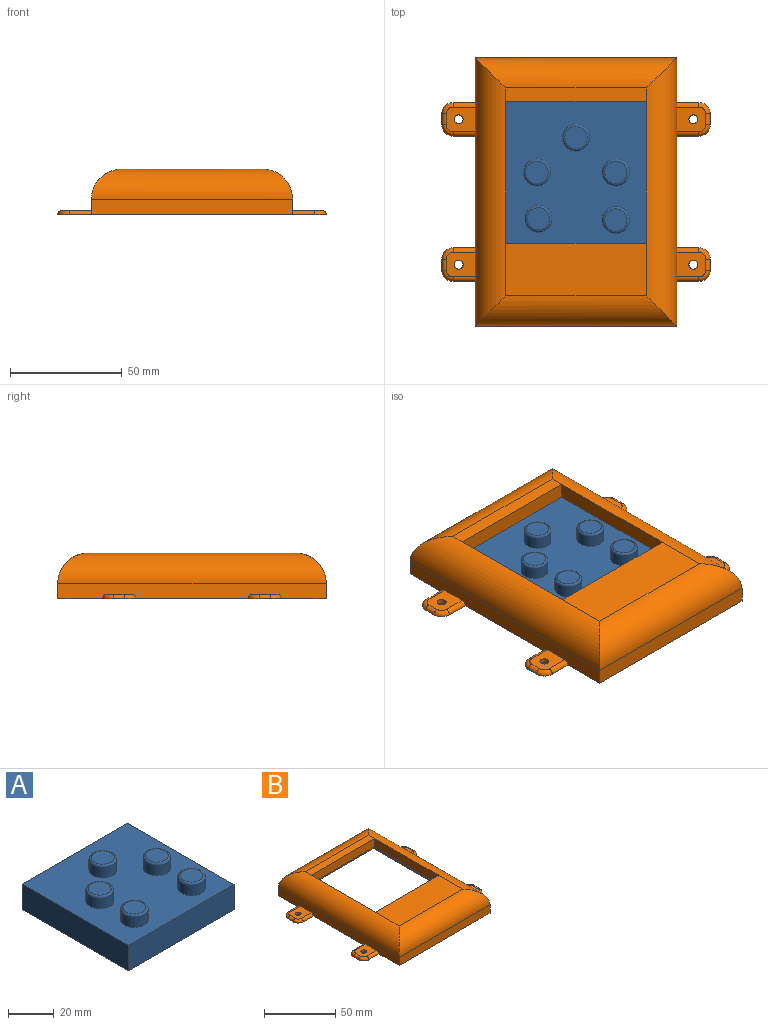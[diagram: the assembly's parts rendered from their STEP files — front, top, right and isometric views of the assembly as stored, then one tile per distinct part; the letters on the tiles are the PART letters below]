
ASSEMBLY  parts=2 mates=1
PART A: 21 faces, bbox 65x65.5x20 mm
  f0: plane 65x13.5mm, normal (0,1,0), area 877.5mm2, adj f1,f3,f4,f5
  f1: plane 65.5x13.5mm, normal (-1,0,0), area 884.3mm2, adj f0,f2,f4,f5
  f2: plane 65x13.5mm, normal (0,-1,0), area 877.5mm2, adj f1,f3,f4,f5
  f3: plane 65.5x13.5mm, normal (1,0,0), area 884.3mm2, adj f0,f2,f4,f5
  f4: plane 65.5x65mm, normal (0,0,1), area 3692mm2, adj f0,f1,f2,f3,f6,f8,f10,f12
  f5: plane 65.5x65mm, normal (0,0,-1), area 4257.5mm2, adj f0,f1,f2,f3
  f6: cylinder r=6mm len=12mm, axis (0,0,-1), area 207.3mm2, adj f4,f20
  f7: plane 10x10mm, normal (0,0,1), area 78.5mm2, adj f20
  f8: cylinder r=6mm len=12mm, axis (0,0,-1), area 207.3mm2, adj f4,f19
  f9: plane 10x10mm, normal (0,0,1), area 78.5mm2, adj f19
  f10: cylinder r=6mm len=12mm, axis (0,0,-1), area 207.3mm2, adj f4,f18
  f11: plane 10x10mm, normal (0,0,1), area 78.5mm2, adj f18
  f12: cylinder r=6mm len=12mm, axis (0,0,-1), area 207.3mm2, adj f4,f17
  f13: plane 10x10mm, normal (0,0,1), area 78.5mm2, adj f17
  f14: cylinder r=6mm len=12mm, axis (0,0,-1), area 207.3mm2, adj f4,f16
  f15: plane 10x10mm, normal (0,0,1), area 78.5mm2, adj f16
  f16: torus R=5mm, axis (0,0,1), area 55.6mm2, adj f14,f15
  f17: torus R=5mm, axis (0,0,1), area 55.6mm2, adj f12,f13
  f18: torus R=5mm, axis (0,0,1), area 55.6mm2, adj f10,f11
  f19: torus R=5mm, axis (0,0,1), area 55.6mm2, adj f8,f9
  f20: torus R=5mm, axis (0,0,1), area 55.6mm2, adj f6,f7
PART B: 63 faces, bbox 120.8x120x21.9 mm
  f0: plane 120x7mm, normal (-1,0,0), area 783.4mm2, adj f1,f13,f14,f18,f53,f54,f55,f56
  f1: plane 120x120mm, normal (0,0,-1), area 1630.8mm2, adj f0,f2,f13,f14,f27,f28,f29,f30
  f2: plane 120x7mm, normal (1,0,0), area 783.4mm2, adj f1,f13,f14,f19,f35,f36,f39,f43
  f3: plane 63x23.5mm, normal (0,0,1), area 1480.5mm2, adj f8,f18,f19,f20
  f4: plane 65x2mm, normal (0,1,0), area 130mm2, adj f5,f7,f15,f16
  f5: plane 65.5x2mm, normal (1,0,0), area 131mm2, adj f4,f6,f15,f16
  f6: plane 65x2mm, normal (0,-1,0), area 130mm2, adj f5,f7,f15,f16
  f7: plane 65.5x2mm, normal (-1,0,0), area 131mm2, adj f4,f6,f15,f16
  f8: plane 63x7mm, normal (0,1,0), area 441mm2, adj f3,f9,f11,f15
  f9: plane 63.5x7mm, normal (-1,0,0), area 444.5mm2, adj f8,f10,f15,f19
  f10: plane 63x7mm, normal (0,-1,0), area 441mm2, adj f9,f11,f12,f15
  f11: plane 63.5x7mm, normal (1,0,0), area 444.5mm2, adj f8,f10,f15,f18
  f12: plane 63x6mm, normal (0,0,1), area 378mm2, adj f10,f17,f18,f19
  f13: plane 90x7mm, normal (0,1,0), area 630mm2, adj f0,f1,f2,f17
  f14: plane 90x7mm, normal (0,-1,0), area 630mm2, adj f0,f1,f2,f20
  f15: plane 65.5x65mm, normal (0,0,-1), area 257mm2, adj f4,f5,f6,f7,f8,f9,f10,f11
  f16: plane 67.5x67mm, normal (0,0,-1), area 265mm2, adj f4,f5,f6,f7,f22,f23,f24,f25
  f17: cylinder r=13.5mm len=90mm, axis (1,0,0), area 1700.5mm2, adj f12,f13,f18,f19
  f18: cylinder r=13.5mm len=120mm, axis (0,1,0), area 2336.6mm2, adj f0,f3,f11,f12,f17,f20
  f19: cylinder r=13.5mm len=120mm, axis (0,-1,0), area 2336.6mm2, adj f2,f3,f9,f12,f17,f20
  f20: cylinder r=13.5mm len=90mm, axis (-1,0,0), area 1700.5mm2, adj f3,f14,f18,f19
  f21: plane 63x21.5mm, normal (0,0,-1), area 1354.5mm2, adj f22,f32,f33,f34
  f22: plane 67x7mm, normal (0,-1,0), area 468.8mm2, adj f16,f21,f23,f25,f32,f33
  f23: plane 67.5x6.82mm, normal (1,0,0), area 460.7mm2, adj f16,f22,f24,f33
  f24: plane 67x7mm, normal (0,1,0), area 468.8mm2, adj f16,f23,f25,f26,f32,f33
  f25: plane 67.5x6.82mm, normal (-1,0,0), area 460.7mm2, adj f16,f22,f24,f32
  f26: plane 63x4mm, normal (0,0,-1), area 252mm2, adj f24,f31,f32,f33
  f27: plane 86x7mm, normal (0,-1,0), area 602mm2, adj f1,f28,f30,f31
  f28: plane 116x7mm, normal (1,0,0), area 812mm2, adj f1,f27,f29,f32
  f29: plane 86x7mm, normal (0,1,0), area 602mm2, adj f1,f28,f30,f34
  f30: plane 116x7mm, normal (-1,0,0), area 812mm2, adj f1,f27,f29,f33
  f31: cylinder r=11.5mm len=86mm, axis (1,0,0), area 1402.5mm2, adj f26,f27,f32,f33
  f32: cylinder r=11.5mm len=116mm, axis (0,1,0), area 1808.8mm2, adj f21,f22,f24,f25,f26,f28,f31,f34
  f33: cylinder r=11.5mm len=116mm, axis (0,-1,0), area 1808.8mm2, adj f21,f22,f23,f24,f26,f30,f31,f34
  f34: cylinder r=11.5mm len=86mm, axis (-1,0,0), area 1402.5mm2, adj f21,f29,f32,f33
  f35: plane 13x11mm, normal (0,0,1), area 126.6mm2, adj f2,f38,f39,f40,f41,f42,f43
  f36: plane 13x11mm, normal (0,0,1), area 126.6mm2, adj f2,f37,f44,f45,f46,f47,f48
  f37: cylinder r=2mm len=4mm, axis (0,0,1), area 25.1mm2, adj f1,f36
  f38: cylinder r=2mm len=4mm, axis (0,0,1), area 25.1mm2, adj f1,f35
  f39: cylinder r=2mm len=10mm, axis (-1,0,0), area 31.4mm2, adj f1,f2,f35,f40
  f40: torus R=3mm, axis (0,0,1), area 21.1mm2, adj f1,f35,f39,f41
  f41: cylinder r=2mm len=5mm, axis (0,1,0), area 15.7mm2, adj f1,f35,f40,f42
  f42: torus R=3mm, axis (0,0,1), area 21.1mm2, adj f1,f35,f41,f43
  f43: cylinder r=2mm len=10mm, axis (1,0,0), area 31.4mm2, adj f1,f2,f35,f42
  f44: cylinder r=2mm len=10mm, axis (1,0,0), area 31.4mm2, adj f1,f2,f36,f45
  f45: torus R=3mm, axis (0,0,-1), area 21.1mm2, adj f1,f36,f44,f46
  f46: cylinder r=2mm len=5mm, axis (0,1,0), area 15.7mm2, adj f1,f36,f45,f47
  f47: torus R=3mm, axis (0,0,-1), area 21.1mm2, adj f1,f36,f46,f48
  f48: cylinder r=2mm len=10mm, axis (-1,0,0), area 31.4mm2, adj f1,f2,f36,f47
  f49: torus R=3mm, axis (0,0,-1), area 21.1mm2, adj f1,f50,f53,f54
  f50: cylinder r=2mm len=5mm, axis (0,1,0), area 15.7mm2, adj f1,f49,f51,f53
  f51: torus R=3mm, axis (0,0,-1), area 21.1mm2, adj f1,f50,f53,f55
  f52: cylinder r=2mm len=4mm, axis (0,0,1), area 25.1mm2, adj f1,f53
  f53: plane 13x11mm, normal (0,0,1), area 126.6mm2, adj f0,f49,f50,f51,f52,f54,f55
  f54: cylinder r=2mm len=10mm, axis (-1,0,0), area 31.4mm2, adj f0,f1,f49,f53
  f55: cylinder r=2mm len=10mm, axis (1,0,0), area 31.4mm2, adj f0,f1,f51,f53
  f56: plane 13x11mm, normal (0,0,1), area 126.6mm2, adj f0,f57,f58,f59,f60,f61,f62
  f57: cylinder r=2mm len=4mm, axis (0,0,1), area 25.1mm2, adj f1,f56
  f58: cylinder r=2mm len=10mm, axis (1,0,0), area 31.4mm2, adj f0,f1,f56,f59
  f59: torus R=3mm, axis (0,0,1), area 21.1mm2, adj f1,f56,f58,f60
  f60: cylinder r=2mm len=5mm, axis (0,1,0), area 15.7mm2, adj f1,f56,f59,f61
  f61: torus R=3mm, axis (0,0,1), area 21.1mm2, adj f1,f56,f60,f62
  f62: cylinder r=2mm len=10mm, axis (-1,0,0), area 31.4mm2, adj f0,f1,f56,f61
PLACE A t=(-18.54,11.24,18.92)mm
PLACE B t=(-18.54,2.49,18.92)mm
MATE fastened A.f4 <-> B.f15  axis (0,0,1) through (-51.04,43.99,32.42)mm
